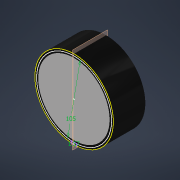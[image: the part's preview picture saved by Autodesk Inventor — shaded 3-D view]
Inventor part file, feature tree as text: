
AUTODESK INVENTOR PART (.ipt)
format: ipt  version: 2021 (Build 250183000, 183)  size: 107,520 bytes
history: native  units: in
note: dims shown in document units (in); Inventor stores cm internally (conversion verified against a paired STEP export)
features: sketch x2, split x1
ambient origin geometry x8: Origin, YZ Plane, XZ Plane, XY Plane, X Axis, Y Axis, Z Axis, Center Point
bodies: Solid2 (feature_tree), Solid1 (feature_tree)
feature tree (3):
  split  "Split1"
  sketch  "Sketch2"
  sketch  "Sketch1"  dims[d0=3.937in]
